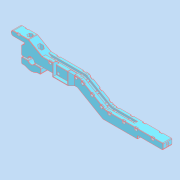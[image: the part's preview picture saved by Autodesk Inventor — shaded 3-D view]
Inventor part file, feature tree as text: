
AUTODESK INVENTOR PART (.ipt)
format: ipt  version: 2021.2 (Build 252289000, 289)  size: 1,148,928 bytes
history: native  units: mm
features: other x7, chamfer x2, fillet x1
ambient origin geometry x8: Origin, YZ Plane, XZ Plane, XY Plane, X Axis, Y Axis, Z Axis, Center Point
bodies: Body1 (feature_tree)
feature tree (10):
  other  "Твёрдое тело.ipt"
  fillet  "Сопряжение4"  Radius=10.0mm
  chamfer  "Фаска3"  Distance=170.5mm
  chamfer  "Фаска4"  Distance=1.0mm
  other  "РабПлоскость2"
  other  "Разделение1"
  other  "Луч::Твёрдое тело.ipt"
  other  "Элемент создания тегов1"
  other  "РабПлоскость1"
  other  "Твердое тело1"
